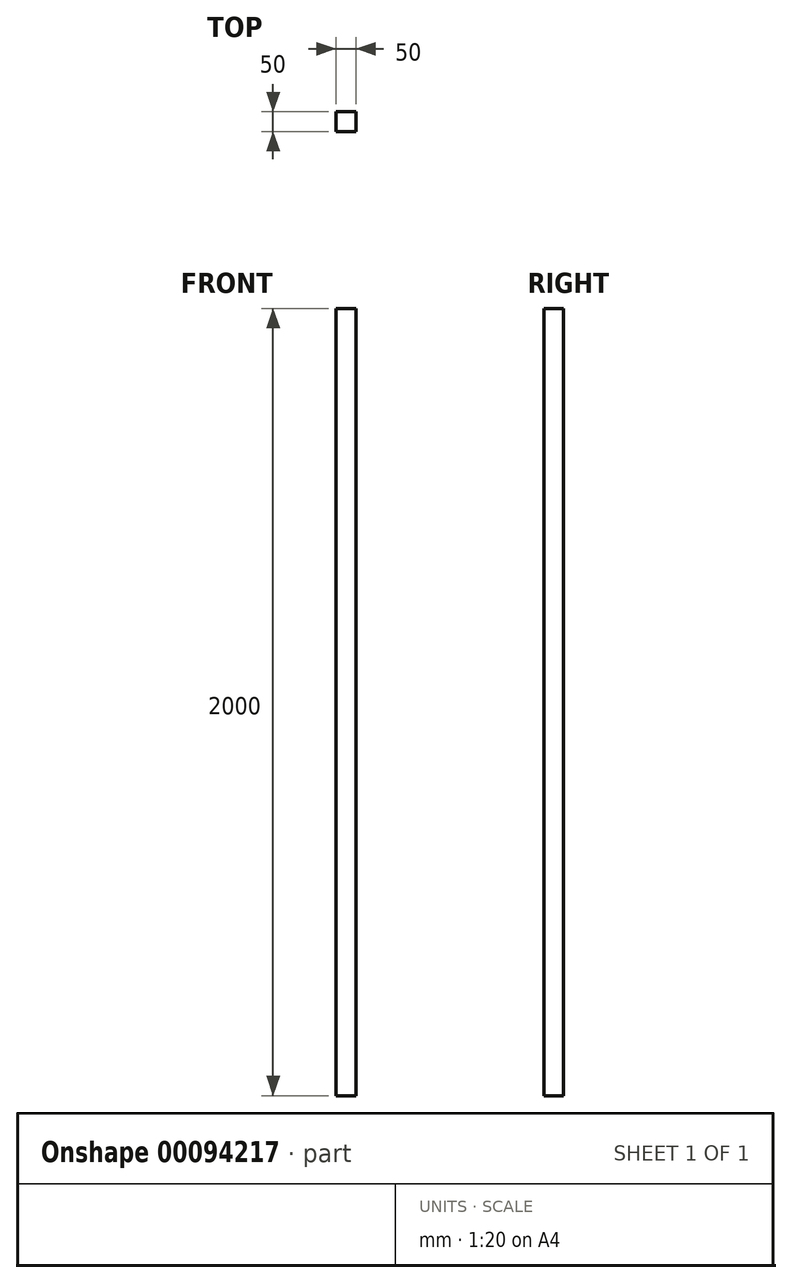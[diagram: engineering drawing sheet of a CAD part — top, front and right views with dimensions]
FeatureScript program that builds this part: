
annotation { "Feature Type Name" : "Feature", "Feature Type Description" : "" }
export const myFeature = defineFeature(function(context is Context, id is Id, definition is map)
    precondition{}
    {
        {
            var Q0;
            Q0=qCreatedBy(makeId("Front.planeOp"),FACE);
            var sketch = newSketch(context, id + "F0", { "sketchPlane" : qUnion([Q0])});
            skLineSegment(sketch, "E0.bottom", {"start": v(25, -1000) * mm, "end": v(-25, -1000) * mm});
            skLineSegment(sketch, "E0.top", {"start": v(25, 1000) * mm, "end": v(-25, 1000) * mm});
            skLineSegment(sketch, "E0.left", {"start": v(25, -1000) * mm, "end": v(25, 1000) * mm});
            skLineSegment(sketch, "E0.right", {"start": v(-25, -1000) * mm, "end": v(-25, 1000) * mm});
            skPoint(sketch, "E0.middle", {"position": v(0, 0) * mm});
            skSolve(sketch);
        }
        {
            var Q0;
            Q0=makeQuery(id+"F0.imprint","IMPRINT",FACE,{"disambiguationData":[TD([[makeQuery(id+"F0.imprint","IMPRINT",EDGE,{"derivedFrom":sQuery(id+"F0.wireOp",EDGE,"E0.bottom")}),-1.0]])]});
            extrude(context, id + "F1", {"entities" : qUnion([Q0]), "endBound" : BoundingType.SYMMETRIC, "depth" : 50 * mm});
        }
    });
